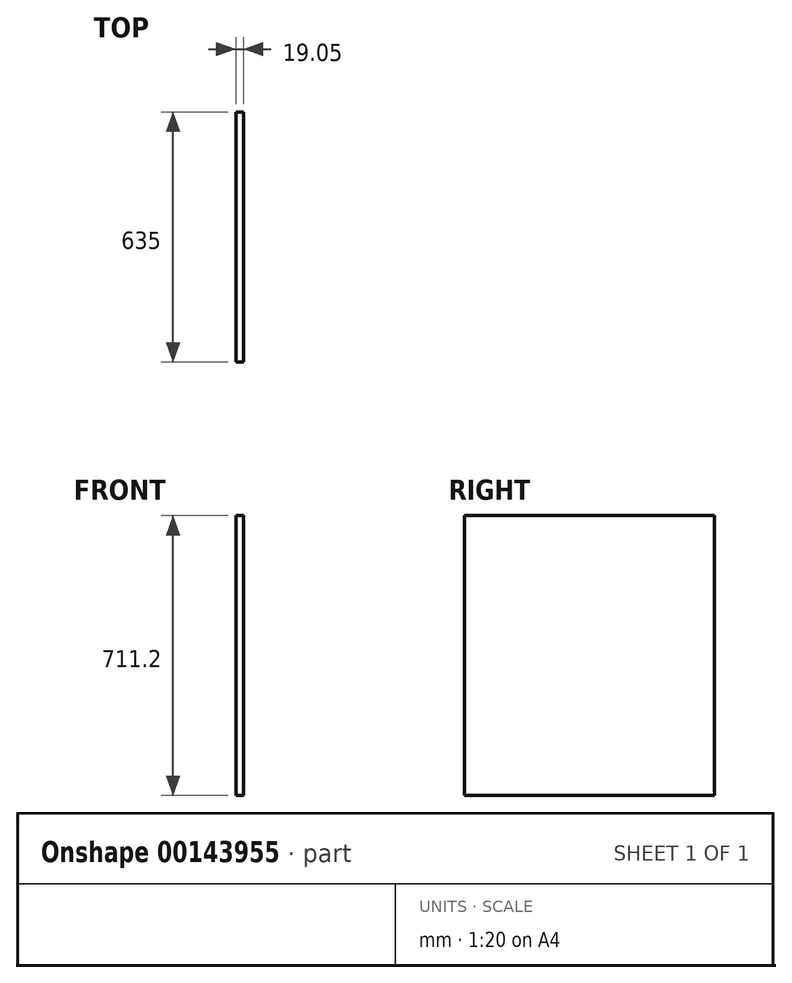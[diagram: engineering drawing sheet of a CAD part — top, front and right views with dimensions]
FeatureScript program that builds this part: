
annotation { "Feature Type Name" : "Feature", "Feature Type Description" : "" }
export const myFeature = defineFeature(function(context is Context, id is Id, definition is map)
    precondition{}
    {
        {
            var Q0;
            Q0=qCreatedBy(makeId("Right.planeOp"),FACE);
            var sketch = newSketch(context, id + "F0", { "sketchPlane" : qUnion([Q0])});
            skLineSegment(sketch, "E0.bottom", {"start": v(-426.54, 576.63) * mm, "end": v(208.46, 576.63) * mm});
            skLineSegment(sketch, "E0.top", {"start": v(-426.54, -134.57) * mm, "end": v(208.46, -134.57) * mm});
            skLineSegment(sketch, "E0.left", {"start": v(-426.54, 576.63) * mm, "end": v(-426.54, -134.57) * mm});
            skLineSegment(sketch, "E0.right", {"start": v(208.46, 576.63) * mm, "end": v(208.46, -134.57) * mm});
            skSolve(sketch);
        }
        {
            var Q0;
            Q0=makeQuery(id+"F0.imprint","IMPRINT",FACE,{"disambiguationData":[TD([[makeQuery(id+"F0.imprint","IMPRINT",EDGE,{"derivedFrom":sQuery(id+"F0.wireOp",EDGE,"E0.bottom")}),-1.0]])]});
            extrude(context, id + "F1", {"entities" : qUnion([Q0]), "depth" : 19.05 * mm});
        }
    });
